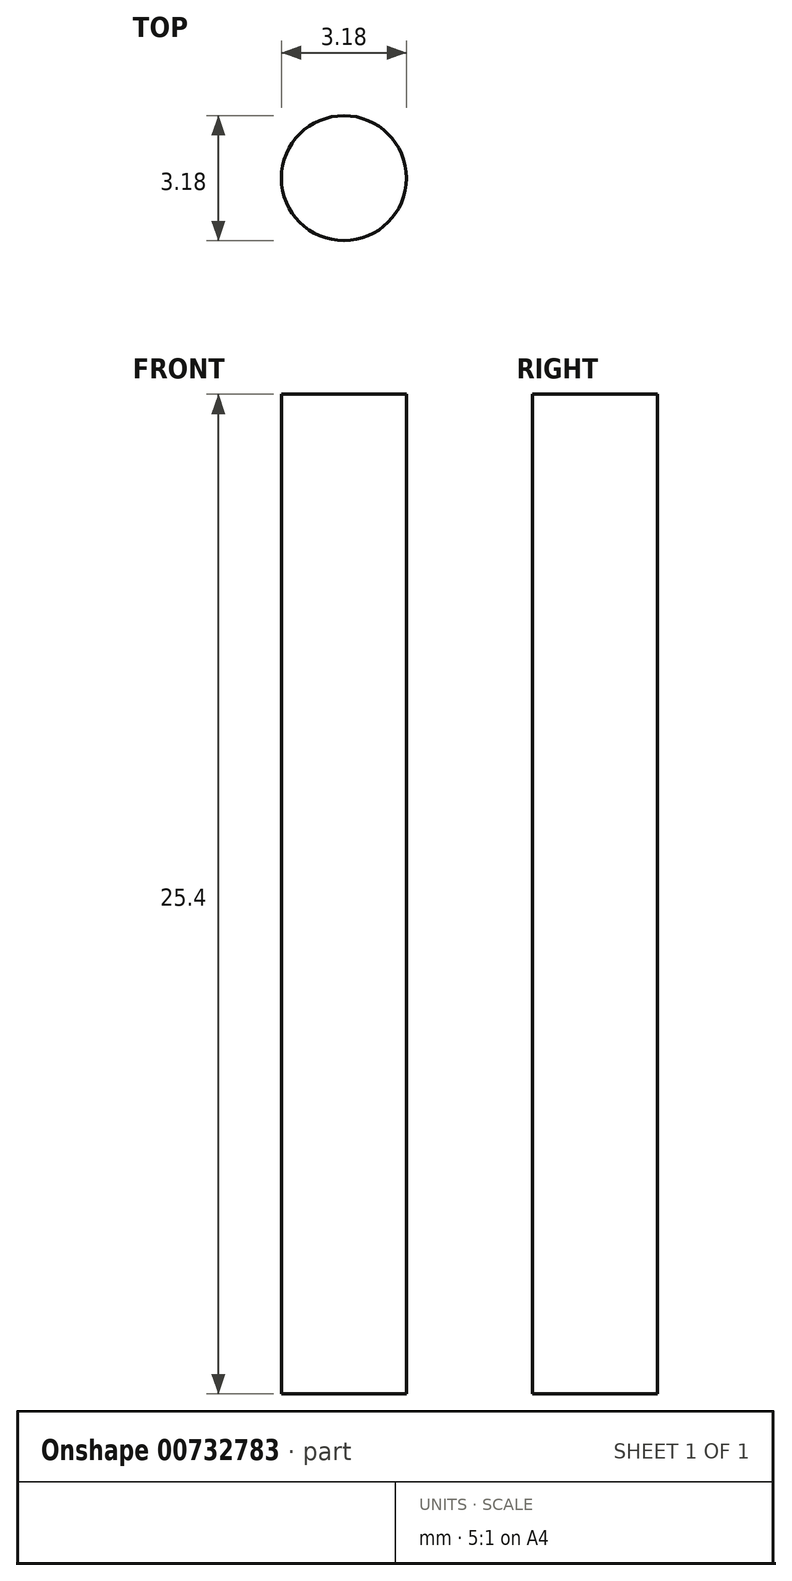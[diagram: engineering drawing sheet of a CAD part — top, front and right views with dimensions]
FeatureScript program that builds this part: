
annotation { "Feature Type Name" : "Feature", "Feature Type Description" : "" }
export const myFeature = defineFeature(function(context is Context, id is Id, definition is map)
    precondition{}
    {
        {
            var Q0;
            Q0=qCreatedBy(makeId("Top.planeOp"),FACE);
            var sketch = newSketch(context, id + "F0", { "sketchPlane" : qUnion([Q0])});
            skCircle(sketch, "E0", {"center": v(0, 0) * mm, "radius": 1.59 * mm});
            skSolve(sketch);
        }
        {
            var Q0;
            Q0 = qSketchRegion(id + "F0", true);
            extrude(context, id + "F1", {"entities" : qUnion([Q0]), "depth" : 25.4 * mm, "offsetDistance" : 25.4 * mm});
        }
    });
